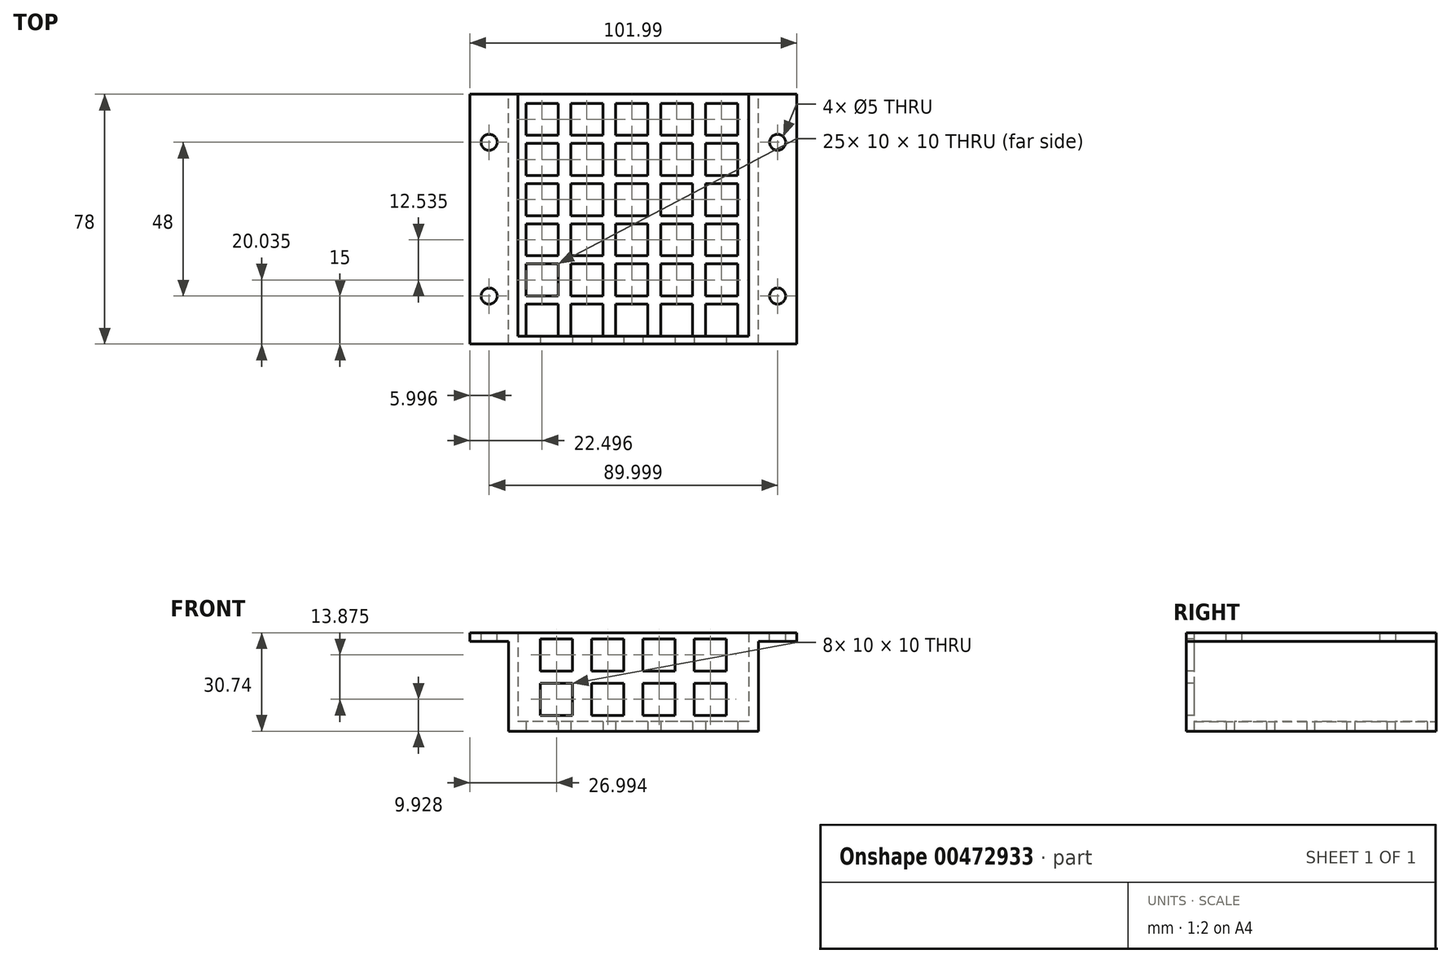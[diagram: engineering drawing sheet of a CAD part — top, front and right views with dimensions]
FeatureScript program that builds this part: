
annotation { "Feature Type Name" : "Feature", "Feature Type Description" : "" }
export const myFeature = defineFeature(function(context is Context, id is Id, definition is map)
    precondition{}
    {
        {
            var Q0;
            Q0=qCreatedBy(makeId("Front.planeOp"),FACE);
            var sketch = newSketch(context, id + "F0", { "sketchPlane" : qUnion([Q0])});
            skLineSegment(sketch, "E0", {"start": v(-2.97, -6.62) * mm, "end": v(-2.97, -9.62) * mm});
            skLineSegment(sketch, "E1", {"start": v(-2.97, -9.62) * mm, "end": v(36.03, -9.62) * mm});
            skLineSegment(sketch, "E2", {"start": v(36.03, -9.62) * mm, "end": v(36.03, 18.38) * mm});
            skLineSegment(sketch, "E3", {"start": v(36.03, 18.38) * mm, "end": v(48.02, 18.38) * mm});
            skLineSegment(sketch, "E4", {"start": v(48.02, 18.38) * mm, "end": v(48.02, 21.12) * mm});
            skLineSegment(sketch, "E5", {"start": v(48.02, 21.12) * mm, "end": v(33.02, 21.12) * mm});
            skLineSegment(sketch, "E6", {"start": v(33.02, 21.12) * mm, "end": v(33.02, -6.62) * mm});
            skLineSegment(sketch, "E7", {"start": v(33.02, -6.62) * mm, "end": v(-2.97, -6.62) * mm});
            skLineSegment(sketch, "E8.MirrorCS", {"start": v(-53.97, 18.38) * mm, "end": v(-53.97, 21.12) * mm});
            skLineSegment(sketch, "E9.MirrorCS", {"start": v(-41.97, -9.62) * mm, "end": v(-41.97, 18.38) * mm});
            skLineSegment(sketch, "E10.MirrorCS", {"start": v(-41.97, 18.38) * mm, "end": v(-53.97, 18.38) * mm});
            skLineSegment(sketch, "E11.MirrorCS", {"start": v(-53.97, 21.12) * mm, "end": v(-38.97, 21.12) * mm});
            skLineSegment(sketch, "E12.MirrorCS", {"start": v(-38.97, 21.12) * mm, "end": v(-38.97, -6.62) * mm});
            skLineSegment(sketch, "E13.MirrorCS", {"start": v(-2.97, -9.62) * mm, "end": v(-41.97, -9.62) * mm});
            skLineSegment(sketch, "E14.MirrorCS", {"start": v(-38.97, -6.62) * mm, "end": v(-2.97, -6.62) * mm});
            skPoint(sketch, "E15.MirrorCS.start.orphan", {"position": v(36.03, 18.38) * mm});
            skSolve(sketch);
        }
        {
            var Q0;
            Q0=qSketchRegion(id+"F0",true);
            extrude(context, id + "F1", {"entities" : qUnion([Q0]), "endBound" : BoundingType.SYMMETRIC, "depth" : 78 * mm});
        }
        {
            var Q0;
            Q0=makeQuery(id+"F1.opExtrude","SWEPT_FACE",FACE,{"disambiguationData":[OSD([sQuery(id+"F0.wireOp",EDGE,"E5")])]});
            var sketch = newSketch(context, id + "F2", { "sketchPlane" : qUnion([Q0])});
            skLineSegment(sketch, "E16", {"start": v(42.02, -39) * mm, "end": v(42.02, 39) * mm, "construction": true});
            skLineSegment(sketch, "E17.0.0", {"start": v(-38.97, 39) * mm, "end": v(-53.97, 39) * mm, "construction": true});
            skLineSegment(sketch, "E17.0.1", {"start": v(-53.97, 39) * mm, "end": v(-53.97, -39) * mm, "construction": true});
            skLineSegment(sketch, "E17.0.2", {"start": v(-53.97, -39) * mm, "end": v(-38.97, -39) * mm, "construction": true});
            skLineSegment(sketch, "E17.0.3", {"start": v(-38.97, -39) * mm, "end": v(-38.97, 39) * mm, "construction": true});
            skLineSegment(sketch, "E18", {"start": v(-47.97, 39) * mm, "end": v(-47.97, -39) * mm, "construction": true});
            skLineSegment(sketch, "E19", {"start": v(-53.97, -24) * mm, "end": v(48.02, -24) * mm, "construction": true});
            skLineSegment(sketch, "E20", {"start": v(48.02, 24) * mm, "end": v(-53.97, 24) * mm, "construction": true});
            skLineSegment(sketch, "E21", {"start": v(48.02, -24) * mm, "end": v(48.02, -39) * mm, "construction": true});
            skLineSegment(sketch, "E22", {"start": v(48.02, 39) * mm, "end": v(48.02, 24) * mm, "construction": true});
            skCircle(sketch, "E23", {"center": v(42.02, -24) * mm, "radius": 2.5 * mm});
            skCircle(sketch, "E24", {"center": v(42.02, 24) * mm, "radius": 2.5 * mm});
            skCircle(sketch, "E25", {"center": v(-47.97, 24) * mm, "radius": 2.5 * mm});
            skCircle(sketch, "E26", {"center": v(-47.97, -24) * mm, "radius": 2.5 * mm});
            skSolve(sketch);
        }
        {
            var Q0;
            Q0=qSketchRegion(id+"F2",true);
            extrude(context, id + "F3", {"entities" : qUnion([Q0]), "operationType" : NewBodyOperationType.REMOVE, "endBound" : BoundingType.UP_TO_NEXT, "oppositeDirection" : true, "depth" : 25 * mm});
        }
        {
            var Q0;
            Q0=makeQuery(id+"F1.opExtrude","SWEPT_FACE",FACE,{"disambiguationData":[OSD([sQuery(id+"F0.wireOp",EDGE,"E1"),sQuery(id+"F0.wireOp",EDGE,"E13.MirrorCS")])]});
            var sketch = newSketch(context, id + "F4", { "sketchPlane" : qUnion([Q0])});
            skLineSegment(sketch, "E27.bottom", {"start": v(-36.47, 36.5) * mm, "end": v(-26.47, 36.5) * mm});
            skLineSegment(sketch, "E27.top", {"start": v(-36.47, 26.5) * mm, "end": v(-26.47, 26.5) * mm});
            skLineSegment(sketch, "E27.left", {"start": v(-36.47, 36.5) * mm, "end": v(-36.47, 26.5) * mm});
            skLineSegment(sketch, "E27.right", {"start": v(-26.47, 36.5) * mm, "end": v(-26.47, 26.5) * mm});
            skLineSegment(sketch, "E28.1.0.0", {"start": v(-22.47, 36.5) * mm, "end": v(-12.47, 36.5) * mm});
            skLineSegment(sketch, "E28.1.0.1", {"start": v(-12.47, 36.5) * mm, "end": v(-12.47, 26.5) * mm});
            skLineSegment(sketch, "E28.1.0.2", {"start": v(-22.47, 36.5) * mm, "end": v(-22.47, 26.5) * mm});
            skLineSegment(sketch, "E28.1.0.3", {"start": v(-22.47, 26.5) * mm, "end": v(-12.47, 26.5) * mm});
            skLineSegment(sketch, "E28.2.0.0", {"start": v(-8.47, 36.5) * mm, "end": v(1.53, 36.5) * mm});
            skLineSegment(sketch, "E28.2.0.1", {"start": v(1.53, 36.5) * mm, "end": v(1.53, 26.5) * mm});
            skLineSegment(sketch, "E28.2.0.2", {"start": v(-8.47, 36.5) * mm, "end": v(-8.47, 26.5) * mm});
            skLineSegment(sketch, "E28.2.0.3", {"start": v(-8.47, 26.5) * mm, "end": v(1.53, 26.5) * mm});
            skLineSegment(sketch, "E28.3.0.0", {"start": v(5.53, 36.5) * mm, "end": v(15.53, 36.5) * mm});
            skLineSegment(sketch, "E28.3.0.1", {"start": v(15.53, 36.5) * mm, "end": v(15.53, 26.5) * mm});
            skLineSegment(sketch, "E28.3.0.2", {"start": v(5.53, 36.5) * mm, "end": v(5.53, 26.5) * mm});
            skLineSegment(sketch, "E28.3.0.3", {"start": v(5.53, 26.5) * mm, "end": v(15.53, 26.5) * mm});
            skLineSegment(sketch, "E28.4.0.0", {"start": v(19.53, 36.5) * mm, "end": v(29.53, 36.5) * mm});
            skLineSegment(sketch, "E28.4.0.1", {"start": v(29.53, 36.5) * mm, "end": v(29.53, 26.5) * mm});
            skLineSegment(sketch, "E28.4.0.2", {"start": v(19.53, 36.5) * mm, "end": v(19.53, 26.5) * mm});
            skLineSegment(sketch, "E28.4.0.3", {"start": v(19.53, 26.5) * mm, "end": v(29.53, 26.5) * mm});
            skLineSegment(sketch, "E28.direction1", {"start": v(-36.47, 36.5) * mm, "end": v(-22.47, 36.5) * mm, "construction": true});
            skLineSegment(sketch, "E29.1.0.0", {"start": v(5.53, 23.97) * mm, "end": v(5.53, 13.97) * mm});
            skLineSegment(sketch, "E29.1.0.1", {"start": v(5.53, 13.97) * mm, "end": v(15.53, 13.97) * mm});
            skLineSegment(sketch, "E29.1.0.2", {"start": v(19.53, 13.97) * mm, "end": v(29.53, 13.97) * mm});
            skLineSegment(sketch, "E29.1.0.3", {"start": v(15.53, 23.97) * mm, "end": v(15.53, 13.97) * mm});
            skLineSegment(sketch, "E29.1.0.4", {"start": v(29.53, 23.97) * mm, "end": v(29.53, 13.97) * mm});
            skLineSegment(sketch, "E29.1.0.5", {"start": v(-36.47, 13.97) * mm, "end": v(-26.47, 13.97) * mm});
            skLineSegment(sketch, "E29.1.0.6", {"start": v(-36.47, 23.97) * mm, "end": v(-36.47, 13.97) * mm});
            skLineSegment(sketch, "E29.1.0.7", {"start": v(-26.47, 23.97) * mm, "end": v(-26.47, 13.97) * mm});
            skLineSegment(sketch, "E29.1.0.8", {"start": v(-22.47, 23.97) * mm, "end": v(-12.47, 23.97) * mm});
            skLineSegment(sketch, "E29.1.0.9", {"start": v(-12.47, 23.97) * mm, "end": v(-12.47, 13.97) * mm});
            skLineSegment(sketch, "E29.1.0.10", {"start": v(-22.47, 23.97) * mm, "end": v(-22.47, 13.97) * mm});
            skLineSegment(sketch, "E29.1.0.11", {"start": v(-22.47, 13.97) * mm, "end": v(-12.47, 13.97) * mm});
            skLineSegment(sketch, "E29.1.0.12", {"start": v(-8.47, 23.97) * mm, "end": v(1.53, 23.97) * mm});
            skLineSegment(sketch, "E29.1.0.13", {"start": v(1.53, 23.97) * mm, "end": v(1.53, 13.97) * mm});
            skLineSegment(sketch, "E29.1.0.14", {"start": v(-8.47, 23.97) * mm, "end": v(-8.47, 13.97) * mm});
            skLineSegment(sketch, "E29.1.0.15", {"start": v(-8.47, 13.97) * mm, "end": v(1.53, 13.97) * mm});
            skLineSegment(sketch, "E29.1.0.16", {"start": v(5.53, 23.97) * mm, "end": v(15.53, 23.97) * mm});
            skLineSegment(sketch, "E29.1.0.17", {"start": v(19.53, 23.97) * mm, "end": v(29.53, 23.97) * mm});
            skLineSegment(sketch, "E29.1.0.18", {"start": v(-36.47, 23.97) * mm, "end": v(-22.47, 23.97) * mm, "construction": true});
            skLineSegment(sketch, "E29.1.0.19", {"start": v(19.53, 23.97) * mm, "end": v(19.53, 13.97) * mm});
            skLineSegment(sketch, "E29.1.0.20", {"start": v(-36.47, 23.97) * mm, "end": v(-26.47, 23.97) * mm});
            skLineSegment(sketch, "E29.2.0.0", {"start": v(5.53, 11.43) * mm, "end": v(5.53, 1.43) * mm});
            skLineSegment(sketch, "E29.2.0.1", {"start": v(5.53, 1.43) * mm, "end": v(15.53, 1.43) * mm});
            skLineSegment(sketch, "E29.2.0.2", {"start": v(19.53, 1.43) * mm, "end": v(29.53, 1.43) * mm});
            skLineSegment(sketch, "E29.2.0.3", {"start": v(15.53, 11.43) * mm, "end": v(15.53, 1.43) * mm});
            skLineSegment(sketch, "E29.2.0.4", {"start": v(29.53, 11.43) * mm, "end": v(29.53, 1.43) * mm});
            skLineSegment(sketch, "E29.2.0.5", {"start": v(-36.47, 1.43) * mm, "end": v(-26.47, 1.43) * mm});
            skLineSegment(sketch, "E29.2.0.6", {"start": v(-36.47, 11.43) * mm, "end": v(-36.47, 1.43) * mm});
            skLineSegment(sketch, "E29.2.0.7", {"start": v(-26.47, 11.43) * mm, "end": v(-26.47, 1.43) * mm});
            skLineSegment(sketch, "E29.2.0.8", {"start": v(-22.47, 11.43) * mm, "end": v(-12.47, 11.43) * mm});
            skLineSegment(sketch, "E29.2.0.9", {"start": v(-12.47, 11.43) * mm, "end": v(-12.47, 1.43) * mm});
            skLineSegment(sketch, "E29.2.0.10", {"start": v(-22.47, 11.43) * mm, "end": v(-22.47, 1.43) * mm});
            skLineSegment(sketch, "E29.2.0.11", {"start": v(-22.47, 1.43) * mm, "end": v(-12.47, 1.43) * mm});
            skLineSegment(sketch, "E29.2.0.12", {"start": v(-8.47, 11.43) * mm, "end": v(1.53, 11.43) * mm});
            skLineSegment(sketch, "E29.2.0.13", {"start": v(1.53, 11.43) * mm, "end": v(1.53, 1.43) * mm});
            skLineSegment(sketch, "E29.2.0.14", {"start": v(-8.47, 11.43) * mm, "end": v(-8.47, 1.43) * mm});
            skLineSegment(sketch, "E29.2.0.15", {"start": v(-8.47, 1.43) * mm, "end": v(1.53, 1.43) * mm});
            skLineSegment(sketch, "E29.2.0.16", {"start": v(5.53, 11.43) * mm, "end": v(15.53, 11.43) * mm});
            skLineSegment(sketch, "E29.2.0.17", {"start": v(19.53, 11.43) * mm, "end": v(29.53, 11.43) * mm});
            skLineSegment(sketch, "E29.2.0.18", {"start": v(-36.47, 11.43) * mm, "end": v(-22.47, 11.43) * mm, "construction": true});
            skLineSegment(sketch, "E29.2.0.19", {"start": v(19.53, 11.43) * mm, "end": v(19.53, 1.43) * mm});
            skLineSegment(sketch, "E29.2.0.20", {"start": v(-36.47, 11.43) * mm, "end": v(-26.47, 11.43) * mm});
            skLineSegment(sketch, "E29.3.0.0", {"start": v(5.53, -1.1) * mm, "end": v(5.53, -11.1) * mm});
            skLineSegment(sketch, "E29.3.0.1", {"start": v(5.53, -11.1) * mm, "end": v(15.53, -11.1) * mm});
            skLineSegment(sketch, "E29.3.0.2", {"start": v(19.53, -11.1) * mm, "end": v(29.53, -11.1) * mm});
            skLineSegment(sketch, "E29.3.0.3", {"start": v(15.53, -1.1) * mm, "end": v(15.53, -11.1) * mm});
            skLineSegment(sketch, "E29.3.0.4", {"start": v(29.53, -1.1) * mm, "end": v(29.53, -11.1) * mm});
            skLineSegment(sketch, "E29.3.0.5", {"start": v(-36.47, -11.1) * mm, "end": v(-26.47, -11.1) * mm});
            skLineSegment(sketch, "E29.3.0.6", {"start": v(-36.47, -1.1) * mm, "end": v(-36.47, -11.1) * mm});
            skLineSegment(sketch, "E29.3.0.7", {"start": v(-26.47, -1.1) * mm, "end": v(-26.47, -11.1) * mm});
            skLineSegment(sketch, "E29.3.0.8", {"start": v(-22.47, -1.1) * mm, "end": v(-12.47, -1.1) * mm});
            skLineSegment(sketch, "E29.3.0.9", {"start": v(-12.47, -1.1) * mm, "end": v(-12.47, -11.1) * mm});
            skLineSegment(sketch, "E29.3.0.10", {"start": v(-22.47, -1.1) * mm, "end": v(-22.47, -11.1) * mm});
            skLineSegment(sketch, "E29.3.0.11", {"start": v(-22.47, -11.1) * mm, "end": v(-12.47, -11.1) * mm});
            skLineSegment(sketch, "E29.3.0.12", {"start": v(-8.47, -1.1) * mm, "end": v(1.53, -1.1) * mm});
            skLineSegment(sketch, "E29.3.0.13", {"start": v(1.53, -1.1) * mm, "end": v(1.53, -11.1) * mm});
            skLineSegment(sketch, "E29.3.0.14", {"start": v(-8.47, -1.1) * mm, "end": v(-8.47, -11.1) * mm});
            skLineSegment(sketch, "E29.3.0.15", {"start": v(-8.47, -11.1) * mm, "end": v(1.53, -11.1) * mm});
            skLineSegment(sketch, "E29.3.0.16", {"start": v(5.53, -1.1) * mm, "end": v(15.53, -1.1) * mm});
            skLineSegment(sketch, "E29.3.0.17", {"start": v(19.53, -1.1) * mm, "end": v(29.53, -1.1) * mm});
            skLineSegment(sketch, "E29.3.0.18", {"start": v(-36.47, -1.1) * mm, "end": v(-22.47, -1.1) * mm, "construction": true});
            skLineSegment(sketch, "E29.3.0.19", {"start": v(19.53, -1.1) * mm, "end": v(19.53, -11.1) * mm});
            skLineSegment(sketch, "E29.3.0.20", {"start": v(-36.47, -1.1) * mm, "end": v(-26.47, -1.1) * mm});
            skLineSegment(sketch, "E29.4.0.0", {"start": v(5.53, -13.64) * mm, "end": v(5.53, -23.64) * mm});
            skLineSegment(sketch, "E29.4.0.1", {"start": v(5.53, -23.64) * mm, "end": v(15.53, -23.64) * mm});
            skLineSegment(sketch, "E29.4.0.2", {"start": v(19.53, -23.64) * mm, "end": v(29.53, -23.64) * mm});
            skLineSegment(sketch, "E29.4.0.3", {"start": v(15.53, -13.64) * mm, "end": v(15.53, -23.64) * mm});
            skLineSegment(sketch, "E29.4.0.4", {"start": v(29.53, -13.64) * mm, "end": v(29.53, -23.64) * mm});
            skLineSegment(sketch, "E29.4.0.5", {"start": v(-36.47, -23.64) * mm, "end": v(-26.47, -23.64) * mm});
            skLineSegment(sketch, "E29.4.0.6", {"start": v(-36.47, -13.64) * mm, "end": v(-36.47, -23.64) * mm});
            skLineSegment(sketch, "E29.4.0.7", {"start": v(-26.47, -13.64) * mm, "end": v(-26.47, -23.64) * mm});
            skLineSegment(sketch, "E29.4.0.8", {"start": v(-22.47, -13.64) * mm, "end": v(-12.47, -13.64) * mm});
            skLineSegment(sketch, "E29.4.0.9", {"start": v(-12.47, -13.64) * mm, "end": v(-12.47, -23.64) * mm});
            skLineSegment(sketch, "E29.4.0.10", {"start": v(-22.47, -13.64) * mm, "end": v(-22.47, -23.64) * mm});
            skLineSegment(sketch, "E29.4.0.11", {"start": v(-22.47, -23.64) * mm, "end": v(-12.47, -23.64) * mm});
            skLineSegment(sketch, "E29.4.0.12", {"start": v(-8.47, -13.64) * mm, "end": v(1.53, -13.64) * mm});
            skLineSegment(sketch, "E29.4.0.13", {"start": v(1.53, -13.64) * mm, "end": v(1.53, -23.64) * mm});
            skLineSegment(sketch, "E29.4.0.14", {"start": v(-8.47, -13.64) * mm, "end": v(-8.47, -23.64) * mm});
            skLineSegment(sketch, "E29.4.0.15", {"start": v(-8.47, -23.64) * mm, "end": v(1.53, -23.64) * mm});
            skLineSegment(sketch, "E29.4.0.16", {"start": v(5.53, -13.64) * mm, "end": v(15.53, -13.64) * mm});
            skLineSegment(sketch, "E29.4.0.17", {"start": v(19.53, -13.64) * mm, "end": v(29.53, -13.64) * mm});
            skLineSegment(sketch, "E29.4.0.18", {"start": v(-36.47, -13.64) * mm, "end": v(-22.47, -13.64) * mm, "construction": true});
            skLineSegment(sketch, "E29.4.0.19", {"start": v(19.53, -13.64) * mm, "end": v(19.53, -23.64) * mm});
            skLineSegment(sketch, "E29.4.0.20", {"start": v(-36.47, -13.64) * mm, "end": v(-26.47, -13.64) * mm});
            skLineSegment(sketch, "E29.direction1", {"start": v(-36.47, 26.5) * mm, "end": v(-36.47, 12.5) * mm, "construction": true});
            skLineSegment(sketch, "E30.0.5.0", {"start": v(5.53, -26.17) * mm, "end": v(5.53, -36.17) * mm});
            skLineSegment(sketch, "E30.3.5.0", {"start": v(5.53, -36.17) * mm, "end": v(15.53, -36.17) * mm});
            skLineSegment(sketch, "E30.6.5.0", {"start": v(19.53, -36.17) * mm, "end": v(29.53, -36.17) * mm});
            skLineSegment(sketch, "E30.9.5.0", {"start": v(15.53, -26.17) * mm, "end": v(15.53, -36.17) * mm});
            skLineSegment(sketch, "E30.12.5.0", {"start": v(29.53, -26.17) * mm, "end": v(29.53, -36.17) * mm});
            skLineSegment(sketch, "E30.15.5.0", {"start": v(-36.47, -36.17) * mm, "end": v(-26.47, -36.17) * mm});
            skLineSegment(sketch, "E30.18.5.0", {"start": v(-36.47, -26.17) * mm, "end": v(-36.47, -36.17) * mm});
            skLineSegment(sketch, "E30.21.5.0", {"start": v(-26.47, -26.17) * mm, "end": v(-26.47, -36.17) * mm});
            skLineSegment(sketch, "E30.24.5.0", {"start": v(-22.47, -26.17) * mm, "end": v(-12.47, -26.17) * mm});
            skLineSegment(sketch, "E30.27.5.0", {"start": v(-12.47, -26.17) * mm, "end": v(-12.47, -36.17) * mm});
            skLineSegment(sketch, "E30.30.5.0", {"start": v(-22.47, -26.17) * mm, "end": v(-22.47, -36.17) * mm});
            skLineSegment(sketch, "E30.33.5.0", {"start": v(-22.47, -36.17) * mm, "end": v(-12.47, -36.17) * mm});
            skLineSegment(sketch, "E30.36.5.0", {"start": v(-8.47, -26.17) * mm, "end": v(1.53, -26.17) * mm});
            skLineSegment(sketch, "E30.39.5.0", {"start": v(1.53, -26.17) * mm, "end": v(1.53, -36.17) * mm});
            skLineSegment(sketch, "E30.42.5.0", {"start": v(-8.47, -26.17) * mm, "end": v(-8.47, -36.17) * mm});
            skLineSegment(sketch, "E30.45.5.0", {"start": v(-8.47, -36.17) * mm, "end": v(1.53, -36.17) * mm});
            skLineSegment(sketch, "E30.48.5.0", {"start": v(5.53, -26.17) * mm, "end": v(15.53, -26.17) * mm});
            skLineSegment(sketch, "E30.51.5.0", {"start": v(19.53, -26.17) * mm, "end": v(29.53, -26.17) * mm});
            skLineSegment(sketch, "E30.54.5.0", {"start": v(-36.47, -26.17) * mm, "end": v(-22.47, -26.17) * mm, "construction": true});
            skLineSegment(sketch, "E30.57.5.0", {"start": v(19.53, -26.17) * mm, "end": v(19.53, -36.17) * mm});
            skLineSegment(sketch, "E30.60.5.0", {"start": v(-36.47, -26.17) * mm, "end": v(-26.47, -26.17) * mm});
            skSolve(sketch);
        }
        {
            var Q0;
            Q0=qSketchRegion(id+"F4",true);
            extrude(context, id + "F5", {"entities" : qUnion([Q0]), "operationType" : NewBodyOperationType.REMOVE, "endBound" : BoundingType.UP_TO_NEXT, "oppositeDirection" : true, "depth" : 25 * mm});
        }
        {
            var Q0;
            Q0=makeQuery(id+"F1.opExtrude","CAP_FACE",FACE,{"disambiguationData":[OSD([sQuery(id+"F0.wireOp",EDGE,"E1"),sQuery(id+"F0.wireOp",EDGE,"E2"),sQuery(id+"F0.wireOp",EDGE,"E3"),sQuery(id+"F0.wireOp",EDGE,"E4"),sQuery(id+"F0.wireOp",EDGE,"E5"),sQuery(id+"F0.wireOp",EDGE,"E6"),sQuery(id+"F0.wireOp",EDGE,"E7"),sQuery(id+"F0.wireOp",EDGE,"E8.MirrorCS"),sQuery(id+"F0.wireOp",EDGE,"E9.MirrorCS"),sQuery(id+"F0.wireOp",EDGE,"E10.MirrorCS"),sQuery(id+"F0.wireOp",EDGE,"E11.MirrorCS"),sQuery(id+"F0.wireOp",EDGE,"E12.MirrorCS"),sQuery(id+"F0.wireOp",EDGE,"E13.MirrorCS"),sQuery(id+"F0.wireOp",EDGE,"E14.MirrorCS")])],"isStart":false});
            var sketch = newSketch(context, id + "F6", { "sketchPlane" : qUnion([Q0])});
            skLineSegment(sketch, "E31.bottom", {"start": v(-38.97, 21.12) * mm, "end": v(33.02, 21.12) * mm});
            skLineSegment(sketch, "E31.top", {"start": v(-38.97, -6.62) * mm, "end": v(33.02, -6.62) * mm});
            skLineSegment(sketch, "E31.left", {"start": v(-38.97, 21.12) * mm, "end": v(-38.97, -6.62) * mm});
            skLineSegment(sketch, "E31.right", {"start": v(33.02, 21.12) * mm, "end": v(33.02, -6.62) * mm});
            skSolve(sketch);
        }
        {
            var Q0;
            Q0=makeQuery(id+"F6.imprint","IMPRINT",FACE,{"disambiguationData":[TD([[makeQuery(id+"F6.imprint","IMPRINT",EDGE,{"derivedFrom":sQuery(id+"F6.wireOp",EDGE,"E31.bottom")}),-1.0]])]});
            extrude(context, id + "F7", {"entities" : qUnion([Q0]), "operationType" : NewBodyOperationType.ADD, "oppositeDirection" : true, "depth" : 2.5 * mm});
        }
        {
            var Q0;
            Q0=makeQuery(id+"F7.boolean.opBoolean","MERGE",FACE,{"derivedFrom":[makeQuery(id+"F1.opExtrude","CAP_FACE",FACE,{"disambiguationData":[OSD([sQuery(id+"F0.wireOp",EDGE,"E1"),sQuery(id+"F0.wireOp",EDGE,"E2"),sQuery(id+"F0.wireOp",EDGE,"E3"),sQuery(id+"F0.wireOp",EDGE,"E4"),sQuery(id+"F0.wireOp",EDGE,"E5"),sQuery(id+"F0.wireOp",EDGE,"E6"),sQuery(id+"F0.wireOp",EDGE,"E7"),sQuery(id+"F0.wireOp",EDGE,"E8.MirrorCS"),sQuery(id+"F0.wireOp",EDGE,"E9.MirrorCS"),sQuery(id+"F0.wireOp",EDGE,"E10.MirrorCS"),sQuery(id+"F0.wireOp",EDGE,"E11.MirrorCS"),sQuery(id+"F0.wireOp",EDGE,"E12.MirrorCS"),sQuery(id+"F0.wireOp",EDGE,"E13.MirrorCS"),sQuery(id+"F0.wireOp",EDGE,"E14.MirrorCS")])],"isStart":false}),makeQuery(id+"F7.opExtrude","CAP_FACE",FACE,{"disambiguationData":[OSD([sQuery(id+"F6.wireOp",EDGE,"E31.bottom"),sQuery(id+"F6.wireOp",EDGE,"E31.top"),sQuery(id+"F6.wireOp",EDGE,"E31.left"),sQuery(id+"F6.wireOp",EDGE,"E31.right")])],"isStart":true})]});
            var sketch = newSketch(context, id + "F8", { "sketchPlane" : qUnion([Q0])});
            skLineSegment(sketch, "E32.bottom", {"start": v(-31.98, 19.18) * mm, "end": v(-21.98, 19.18) * mm});
            skLineSegment(sketch, "E32.top", {"start": v(-31.98, 9.18) * mm, "end": v(-21.98, 9.18) * mm});
            skLineSegment(sketch, "E32.left", {"start": v(-31.98, 19.18) * mm, "end": v(-31.98, 9.18) * mm});
            skLineSegment(sketch, "E32.right", {"start": v(-21.98, 19.18) * mm, "end": v(-21.98, 9.18) * mm});
            skLineSegment(sketch, "E33.1.0.0", {"start": v(-15.98, 19.18) * mm, "end": v(-5.98, 19.18) * mm});
            skLineSegment(sketch, "E33.1.0.1", {"start": v(-5.98, 19.18) * mm, "end": v(-5.98, 9.18) * mm});
            skLineSegment(sketch, "E33.1.0.2", {"start": v(-15.98, 19.18) * mm, "end": v(-15.98, 9.18) * mm});
            skLineSegment(sketch, "E33.1.0.3", {"start": v(-15.98, 9.18) * mm, "end": v(-5.98, 9.18) * mm});
            skLineSegment(sketch, "E33.2.0.0", {"start": v(0.02, 19.18) * mm, "end": v(10.02, 19.18) * mm});
            skLineSegment(sketch, "E33.2.0.1", {"start": v(10.02, 19.18) * mm, "end": v(10.02, 9.18) * mm});
            skLineSegment(sketch, "E33.2.0.2", {"start": v(0.02, 19.18) * mm, "end": v(0.02, 9.18) * mm});
            skLineSegment(sketch, "E33.2.0.3", {"start": v(0.02, 9.18) * mm, "end": v(10.02, 9.18) * mm});
            skLineSegment(sketch, "E33.3.0.0", {"start": v(16.02, 19.18) * mm, "end": v(26.02, 19.18) * mm});
            skLineSegment(sketch, "E33.3.0.1", {"start": v(26.02, 19.18) * mm, "end": v(26.02, 9.18) * mm});
            skLineSegment(sketch, "E33.3.0.2", {"start": v(16.02, 19.18) * mm, "end": v(16.02, 9.18) * mm});
            skLineSegment(sketch, "E33.3.0.3", {"start": v(16.02, 9.18) * mm, "end": v(26.02, 9.18) * mm});
            skLineSegment(sketch, "E33.direction1", {"start": v(-31.98, 19.18) * mm, "end": v(-15.98, 19.18) * mm, "construction": true});
            skLineSegment(sketch, "E34.1.0.0", {"start": v(16.02, 5.3) * mm, "end": v(16.02, -4.7) * mm});
            skLineSegment(sketch, "E34.1.0.1", {"start": v(16.02, -4.7) * mm, "end": v(26.02, -4.7) * mm});
            skLineSegment(sketch, "E34.1.0.3", {"start": v(26.02, 5.3) * mm, "end": v(26.02, -4.7) * mm});
            skLineSegment(sketch, "E34.1.0.5", {"start": v(-31.98, -4.7) * mm, "end": v(-21.98, -4.7) * mm});
            skLineSegment(sketch, "E34.1.0.6", {"start": v(-31.98, 5.3) * mm, "end": v(-31.98, -4.7) * mm});
            skLineSegment(sketch, "E34.1.0.7", {"start": v(-21.98, 5.3) * mm, "end": v(-21.98, -4.7) * mm});
            skLineSegment(sketch, "E34.1.0.8", {"start": v(-15.98, 5.3) * mm, "end": v(-5.98, 5.3) * mm});
            skLineSegment(sketch, "E34.1.0.9", {"start": v(-5.98, 5.3) * mm, "end": v(-5.98, -4.7) * mm});
            skLineSegment(sketch, "E34.1.0.10", {"start": v(-15.98, 5.3) * mm, "end": v(-15.98, -4.7) * mm});
            skLineSegment(sketch, "E34.1.0.11", {"start": v(-15.98, -4.7) * mm, "end": v(-5.98, -4.7) * mm});
            skLineSegment(sketch, "E34.1.0.12", {"start": v(0.02, 5.3) * mm, "end": v(10.02, 5.3) * mm});
            skLineSegment(sketch, "E34.1.0.13", {"start": v(10.02, 5.3) * mm, "end": v(10.02, -4.7) * mm});
            skLineSegment(sketch, "E34.1.0.14", {"start": v(0.02, 5.3) * mm, "end": v(0.02, -4.7) * mm});
            skLineSegment(sketch, "E34.1.0.15", {"start": v(0.02, -4.7) * mm, "end": v(10.02, -4.7) * mm});
            skLineSegment(sketch, "E34.1.0.16", {"start": v(16.02, 5.3) * mm, "end": v(26.02, 5.3) * mm});
            skLineSegment(sketch, "E34.1.0.18", {"start": v(-31.98, 5.3) * mm, "end": v(-15.98, 5.3) * mm, "construction": true});
            skLineSegment(sketch, "E34.1.0.20", {"start": v(-31.98, 5.3) * mm, "end": v(-21.98, 5.3) * mm});
            skLineSegment(sketch, "E34.direction1", {"start": v(-31.98, 19.18) * mm, "end": v(-31.98, 5.3) * mm, "construction": true});
            skSolve(sketch);
        }
        {
            var Q0;
            Q0 = qSketchRegion(id + "F8", true);
            extrude(context, id + "F9", {"entities" : qUnion([Q0]), "operationType" : NewBodyOperationType.REMOVE, "endBound" : BoundingType.UP_TO_NEXT, "oppositeDirection" : true, "depth" : 25 * mm});
        }
    });
